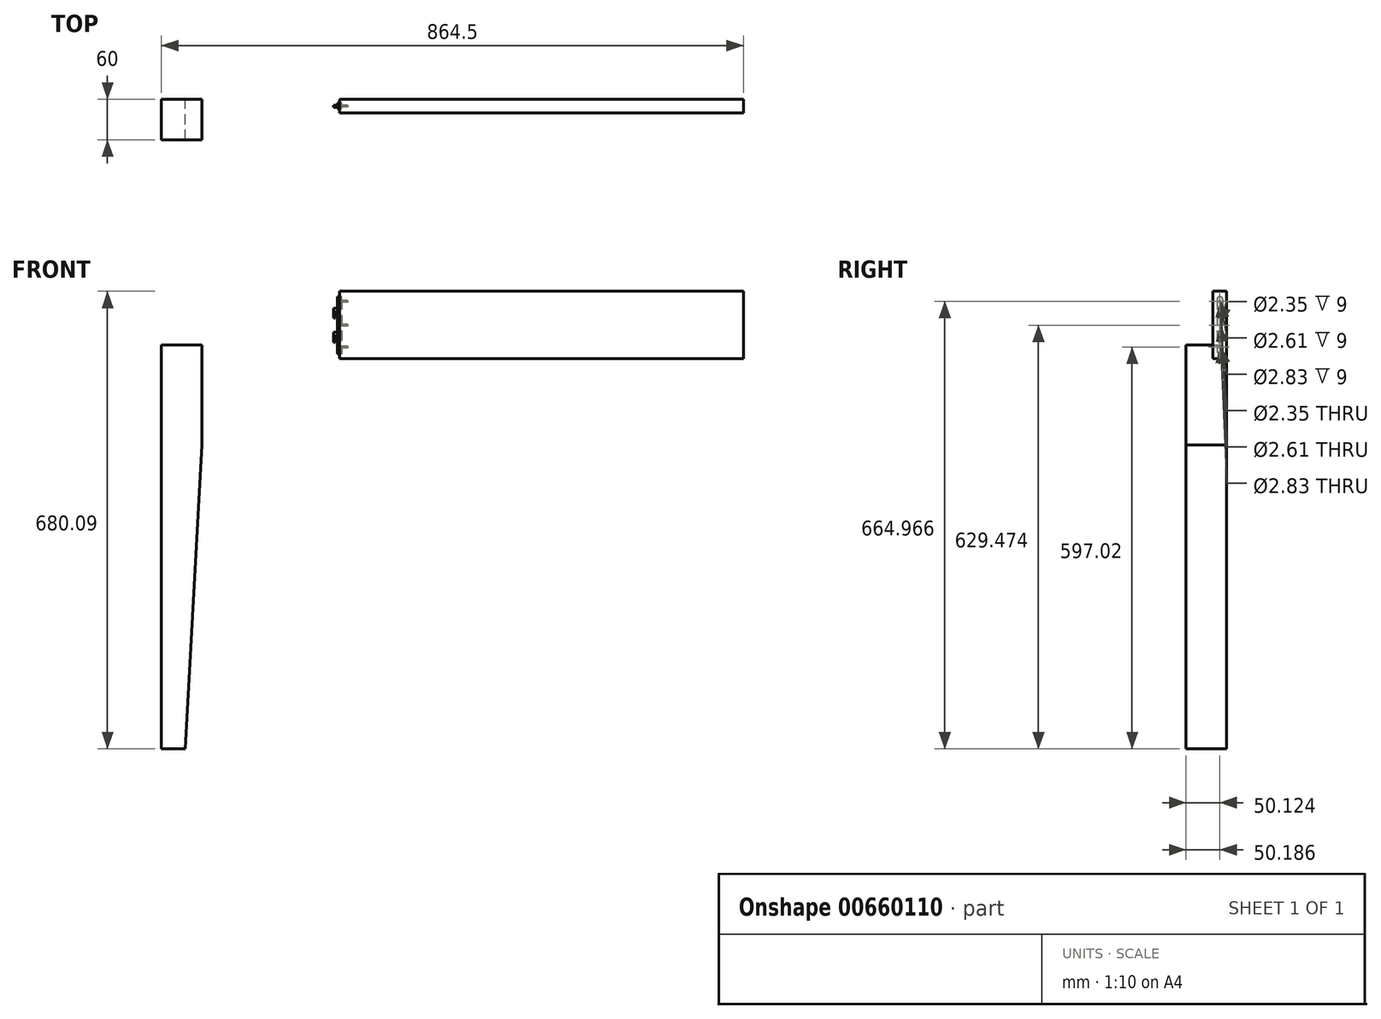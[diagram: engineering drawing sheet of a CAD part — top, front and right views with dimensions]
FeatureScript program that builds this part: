
annotation { "Feature Type Name" : "Feature", "Feature Type Description" : "" }
export const myFeature = defineFeature(function(context is Context, id is Id, definition is map)
    precondition{}
    {
        {
            var Q0;
            Q0=qCreatedBy(makeId("Front.planeOp"),FACE);
            var sketch = newSketch(context, id + "F0", { "sketchPlane" : qUnion([Q0])});
            skLineSegment(sketch, "E0", {"start": v(0, 0) * mm, "end": v(0, 600) * mm});
            skLineSegment(sketch, "E1", {"start": v(0, 600) * mm, "end": v(60, 600) * mm});
            skLineSegment(sketch, "E2", {"start": v(60, 600) * mm, "end": v(60, 451.65) * mm});
            skLineSegment(sketch, "E3", {"start": v(0, 0) * mm, "end": v(35, 0) * mm});
            skLineSegment(sketch, "E4", {"start": v(35, 0) * mm, "end": v(60, 451.65) * mm});
            skSolve(sketch);
        }
        {
            var Q0;
            Q0 = qSketchRegion(id + "F0", true);
            extrude(context, id + "F1", {"entities" : qUnion([Q0]), "depth" : 60 * mm, "offsetDistance" : 25.4 * mm});
        }
        {
            var Q0;
            Q0=qCreatedBy(makeId("Front.planeOp"),FACE);
            var sketch = newSketch(context, id + "F2", { "sketchPlane" : qUnion([Q0])});
            skLineSegment(sketch, "E5.bottom", {"start": v(264.5, 680.09) * mm, "end": v(864.5, 680.09) * mm});
            skLineSegment(sketch, "E5.top", {"start": v(264.5, 580.09) * mm, "end": v(864.5, 580.09) * mm});
            skLineSegment(sketch, "E5.left", {"start": v(264.5, 680.09) * mm, "end": v(264.5, 580.09) * mm});
            skLineSegment(sketch, "E5.right", {"start": v(864.5, 680.09) * mm, "end": v(864.5, 580.09) * mm});
            skSolve(sketch);
        }
        {
            var Q0;
            Q0 = qSketchRegion(id + "F2", true);
            var sketch = newSketch(context, id + "F3", { "sketchPlane" : qUnion([Q0])});
            skSolve(sketch);
        }
        {
            var Q0;
            Q0=makeQuery(id+"F3.imprint","IMPRINT",FACE,{"disambiguationData":[TD([[makeQuery(id+"F3.imprint","IMPRINT",EDGE,{"derivedFrom":makeQuery(id+"F2.imprint","IMPRINT",EDGE,{"derivedFrom":sQuery(id+"F2.wireOp",EDGE,"E5.bottom")})}),-1.0]])]});
            extrude(context, id + "F4", {"entities" : qUnion([Q0]), "depth" : 20 * mm, "offsetDistance" : 25.4 * mm});
        }
        {
            var Q0;
            Q0=makeQuery(id+"F4.opExtrude","SWEPT_FACE",FACE,{"disambiguationData":[OSD([sQuery(id+"F2.wireOp",EDGE,"E5.left")])]});
            var sketch = newSketch(context, id + "F5", { "sketchPlane" : qUnion([Q0])});
            skLineSegment(sketch, "E6", {"start": v(5.7, 667.78) * mm, "end": v(5.7, 591.17) * mm});
            skLineSegment(sketch, "E7", {"start": v(13.93, 667.78) * mm, "end": v(13.93, 591.17) * mm});
            skArc(sketch, "E8", {"start": v(5.7, 667.78) * mm, "mid": v(9.81, 671.9) * mm, "end": v(13.93, 667.78) * mm});
            skArc(sketch, "E9", {"start": v(5.7, 591.17) * mm, "mid": v(9.81, 587.05) * mm, "end": v(13.93, 591.17) * mm});
            skSolve(sketch);
        }
        {
            var Q0;
            Q0=makeQuery(id+"F5.imprint","IMPRINT",FACE,{"disambiguationData":[TD([[makeQuery(id+"F5.imprint","IMPRINT",EDGE,{"derivedFrom":sQuery(id+"F5.wireOp",EDGE,"E6")}),1.0]])]});
            extrude(context, id + "F6", {"entities" : qUnion([Q0]), "operationType" : NewBodyOperationType.REMOVE, "oppositeDirection" : true, "depth" : 3 * mm, "offsetDistance" : 25.4 * mm});
        }
        {
            var Q0;
            Q0 = qSketchRegion(id + "F5", true);
            var Q1;
            Q1=makeQuery(id+"F5.imprint","IMPRINT",FACE,{"disambiguationData":[TD([[makeQuery(id+"F5.imprint","IMPRINT",EDGE,{"derivedFrom":sQuery(id+"F5.wireOp",EDGE,"E6")}),1.0]])]});
            extrude(context, id + "F7", {"entities" : qUnion([Q0, Q1]), "depth" : 3 * mm, "offsetDistance" : 25.4 * mm});
        }
        {
            var Q0;
            Q0=makeQuery(id+"F7.opExtrude","CAP_FACE",FACE,{"disambiguationData":[OSD([sQuery(id+"F5.wireOp",EDGE,"E6"),sQuery(id+"F5.wireOp",EDGE,"E7"),sQuery(id+"F5.wireOp",EDGE,"E8"),sQuery(id+"F5.wireOp",EDGE,"E9")])],"isStart":false});
            var sketch = newSketch(context, id + "F8", { "sketchPlane" : qUnion([Q0])});
            skCircle(sketch, "E10", {"center": v(9.88, 664.97) * mm, "radius": 1.3 * mm});
            skCircle(sketch, "E11", {"center": v(9.81, 629.47) * mm, "radius": 1.18 * mm});
            skPoint(sketch, "E11.centerSnap0", {"position": v(9.81, 671.9) * mm});
            skPoint(sketch, "E11.centerSnap1", {"position": v(13.93, 629.47) * mm});
            skCircle(sketch, "E12", {"center": v(9.88, 597.02) * mm, "radius": 1.41 * mm});
            skSolve(sketch);
        }
        {
            var Q0;
            Q0=makeQuery(id+"F8.imprint","IMPRINT",FACE,{"disambiguationData":[TD([[makeQuery(id+"F8.imprint","IMPRINT",EDGE,{"derivedFrom":sQuery(id+"F8.wireOp",EDGE,"E12")}),1.0]])]});
            var Q1;
            Q1=makeQuery(id+"F8.imprint","IMPRINT",FACE,{"disambiguationData":[TD([[makeQuery(id+"F8.imprint","IMPRINT",EDGE,{"derivedFrom":sQuery(id+"F8.wireOp",EDGE,"E10")}),1.0]])]});
            var Q2;
            Q2=makeQuery(id+"F8.imprint","IMPRINT",FACE,{"disambiguationData":[TD([[makeQuery(id+"F8.imprint","IMPRINT",EDGE,{"derivedFrom":sQuery(id+"F8.wireOp",EDGE,"E11")}),1.0]])]});
            extrude(context, id + "F9", {"entities" : qUnion([Q0, Q1, Q2]), "operationType" : NewBodyOperationType.REMOVE, "oppositeDirection" : true, "depth" : 15 * mm, "offsetDistance" : 25.4 * mm});
        }
        {
            var Q0;
            Q0=makeQuery(id+"F7.opExtrude","CAP_FACE",FACE,{"disambiguationData":[OSD([sQuery(id+"F5.wireOp",EDGE,"E6"),sQuery(id+"F5.wireOp",EDGE,"E7"),sQuery(id+"F5.wireOp",EDGE,"E8"),sQuery(id+"F5.wireOp",EDGE,"E9")])],"isStart":false});
            var sketch = newSketch(context, id + "F10", { "sketchPlane" : qUnion([Q0])});
            skLineSegment(sketch, "E13.bottom", {"start": v(8.64, 655.04) * mm, "end": v(11.44, 655.04) * mm});
            skLineSegment(sketch, "E13.top", {"start": v(8.64, 640.3) * mm, "end": v(11.44, 640.3) * mm});
            skLineSegment(sketch, "E13.left", {"start": v(8.64, 655.04) * mm, "end": v(8.64, 640.3) * mm});
            skLineSegment(sketch, "E13.right", {"start": v(11.44, 655.04) * mm, "end": v(11.44, 640.3) * mm});
            skLineSegment(sketch, "E14.bottom", {"start": v(8.44, 619.4) * mm, "end": v(11.72, 619.4) * mm});
            skLineSegment(sketch, "E14.top", {"start": v(8.44, 604.22) * mm, "end": v(11.72, 604.22) * mm});
            skLineSegment(sketch, "E14.left", {"start": v(8.44, 619.4) * mm, "end": v(8.44, 604.22) * mm});
            skLineSegment(sketch, "E14.right", {"start": v(11.72, 619.4) * mm, "end": v(11.72, 604.22) * mm});
            skSolve(sketch);
        }
        {
            var Q0;
            Q0=makeQuery(id+"F10.imprint","IMPRINT",FACE,{"disambiguationData":[TD([[makeQuery(id+"F10.imprint","IMPRINT",EDGE,{"derivedFrom":sQuery(id+"F10.wireOp",EDGE,"E13.bottom")}),-1.0]])]});
            extrude(context, id + "F11", {"entities" : qUnion([Q0]), "operationType" : NewBodyOperationType.ADD, "depth" : 6 * mm, "offsetDistance" : 25.4 * mm});
        }
        {
            var Q0;
            Q0=makeQuery(id+"F10.imprint","IMPRINT",FACE,{"disambiguationData":[TD([[makeQuery(id+"F10.imprint","IMPRINT",EDGE,{"derivedFrom":sQuery(id+"F10.wireOp",EDGE,"E14.bottom")}),-1.0]])]});
            extrude(context, id + "F12", {"entities" : qUnion([Q0]), "operationType" : NewBodyOperationType.ADD, "depth" : 6 * mm, "offsetDistance" : 25.4 * mm});
        }
        {
            var Q0;
            Q0=makeQuery(id+"F11.opExtrude","SWEPT_FACE",FACE,{"disambiguationData":[OSD([sQuery(id+"F10.wireOp",EDGE,"E13.left")])]});
            var sketch = newSketch(context, id + "F13", { "sketchPlane" : qUnion([Q0])});
            skLineSegment(sketch, "E15.bottom", {"start": v(-261.5, 640.3) * mm, "end": v(-258.44, 640.3) * mm});
            skLineSegment(sketch, "E15.top", {"start": v(-261.5, 648.76) * mm, "end": v(-258.44, 648.76) * mm});
            skLineSegment(sketch, "E15.left", {"start": v(-261.5, 640.3) * mm, "end": v(-261.5, 648.76) * mm});
            skLineSegment(sketch, "E15.right", {"start": v(-258.44, 640.3) * mm, "end": v(-258.44, 648.76) * mm});
            skSolve(sketch);
        }
        {
            var Q0;
            Q0=makeQuery(id+"F13.imprint","IMPRINT",FACE,{"disambiguationData":[TD([[makeQuery(id+"F13.imprint","IMPRINT",EDGE,{"derivedFrom":sQuery(id+"F13.wireOp",EDGE,"E15.bottom")}),-1.0]])]});
            extrude(context, id + "F14", {"entities" : qUnion([Q0]), "operationType" : NewBodyOperationType.REMOVE, "oppositeDirection" : true, "depth" : 25.4 * mm, "offsetDistance" : 25.4 * mm});
        }
        {
            var Q0;
            Q0=makeQuery(id+"F12.opExtrude","SWEPT_FACE",FACE,{"disambiguationData":[OSD([sQuery(id+"F10.wireOp",EDGE,"E14.left")])]});
            var sketch = newSketch(context, id + "F15", { "sketchPlane" : qUnion([Q0])});
            skLineSegment(sketch, "E16.bottom", {"start": v(-261.5, 604.22) * mm, "end": v(-258.01, 604.22) * mm});
            skLineSegment(sketch, "E16.top", {"start": v(-261.5, 613.32) * mm, "end": v(-258.01, 613.32) * mm});
            skLineSegment(sketch, "E16.left", {"start": v(-261.5, 604.22) * mm, "end": v(-261.5, 613.32) * mm});
            skLineSegment(sketch, "E16.right", {"start": v(-258.01, 604.22) * mm, "end": v(-258.01, 613.32) * mm});
            skSolve(sketch);
        }
        {
            var Q0;
            Q0 = qSketchRegion(id + "F15", true);
            extrude(context, id + "F16", {"entities" : qUnion([Q0]), "operationType" : NewBodyOperationType.REMOVE, "oppositeDirection" : true, "depth" : 25.4 * mm, "offsetDistance" : 25.4 * mm});
        }
    });
